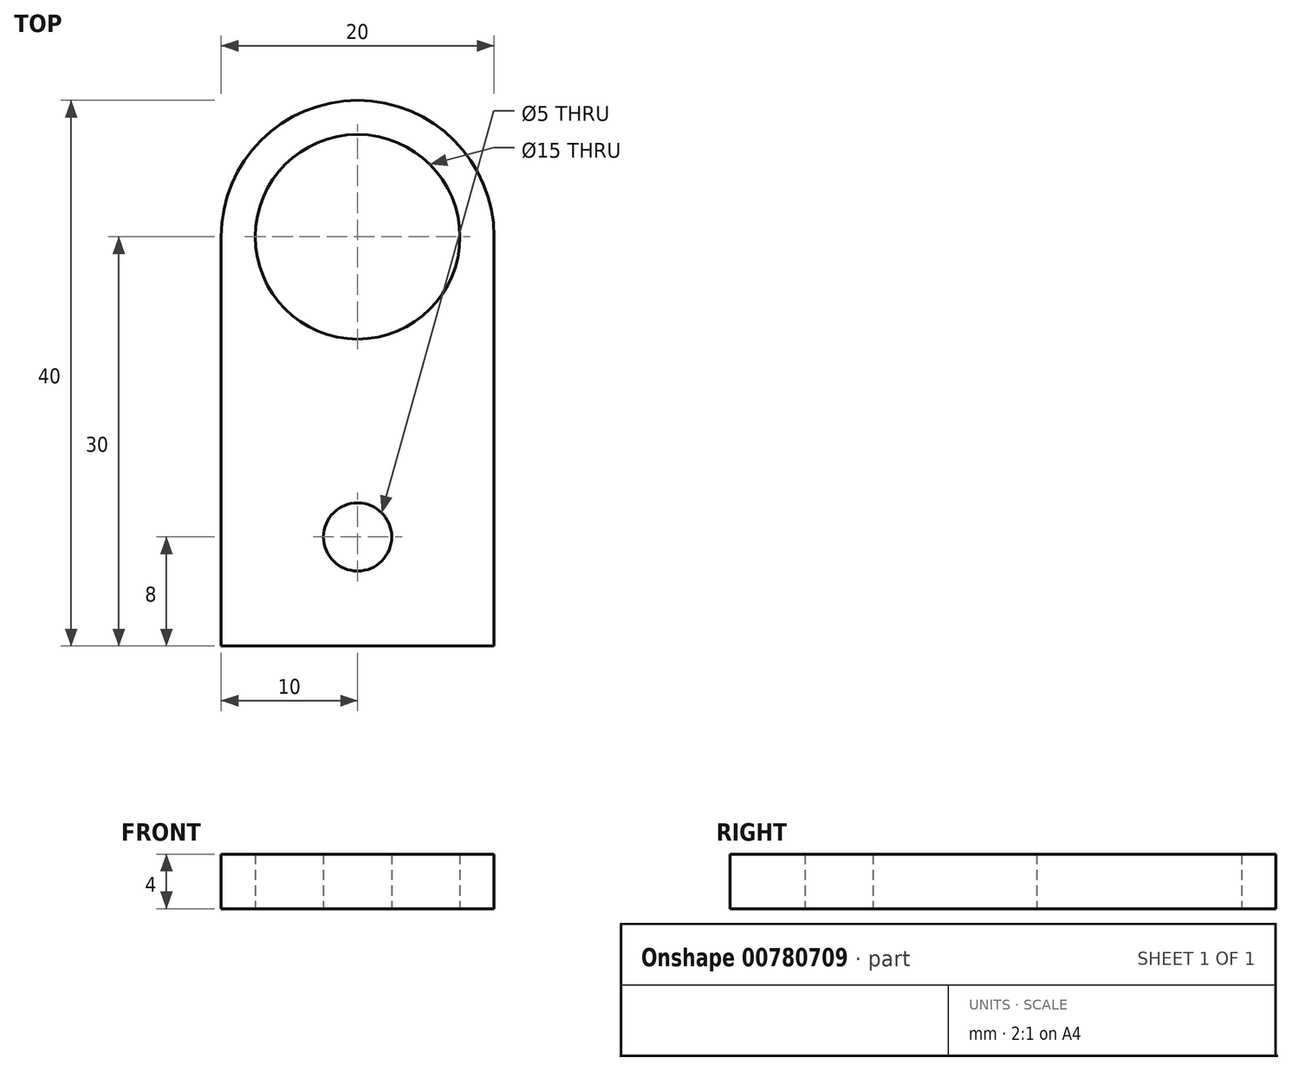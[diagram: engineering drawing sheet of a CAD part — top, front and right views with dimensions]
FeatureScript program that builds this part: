
annotation { "Feature Type Name" : "Feature", "Feature Type Description" : "" }
export const myFeature = defineFeature(function(context is Context, id is Id, definition is map)
    precondition{}
    {
        {
            var Q0;
            Q0=qCreatedBy(makeId("Top.planeOp"),FACE);
            var sketch = newSketch(context, id + "F0", { "sketchPlane" : qUnion([Q0])});
            skLineSegment(sketch, "E0.bottom", {"start": v(0, 0) * mm, "end": v(20, 0) * mm});
            skLineSegment(sketch, "E0.top", {"start": v(0, 40) * mm, "end": v(20, 40) * mm});
            skLineSegment(sketch, "E0.left", {"start": v(0, 0) * mm, "end": v(0, 40) * mm});
            skLineSegment(sketch, "E0.right", {"start": v(20, 0) * mm, "end": v(20, 40) * mm});
            skCircle(sketch, "E1", {"center": v(10, 8) * mm, "radius": 2.5 * mm});
            skCircle(sketch, "E2", {"center": v(10, 30) * mm, "radius": 7.5 * mm});
            skSolve(sketch);
        }
        {
            var Q0;
            Q0=makeQuery(id+"F0.imprint","IMPRINT",FACE,{"disambiguationData":[TD([[makeQuery(id+"F0.imprint","IMPRINT",EDGE,{"derivedFrom":sQuery(id+"F0.wireOp",EDGE,"E0.bottom")}),1.0]])]});
            extrude(context, id + "F1", {"entities" : qUnion([Q0]), "depth" : 4 * mm, "offsetDistance" : 25 * mm});
        }
        {
            var Q0;
            Q0=makeQuery(id+"F1.opExtrude","SWEPT_EDGE",EDGE,{"disambiguationData":[OSD([sQuery(id+"F0.wireOp",EDGE,"E0.top"),sQuery(id+"F0.wireOp",EDGE,"E0.right")])]});
            var Q1;
            Q1=makeQuery(id+"F1.opExtrude","SWEPT_EDGE",EDGE,{"disambiguationData":[OSD([sQuery(id+"F0.wireOp",EDGE,"E0.top"),sQuery(id+"F0.wireOp",EDGE,"E0.left")])]});
            fillet(context, id + "F2", {"entities" : qUnion([Q0, Q1]), "radius" : 10 * mm, "tangentPropagation" : true, "allowEdgeOverflow" : false});
        }
    });
